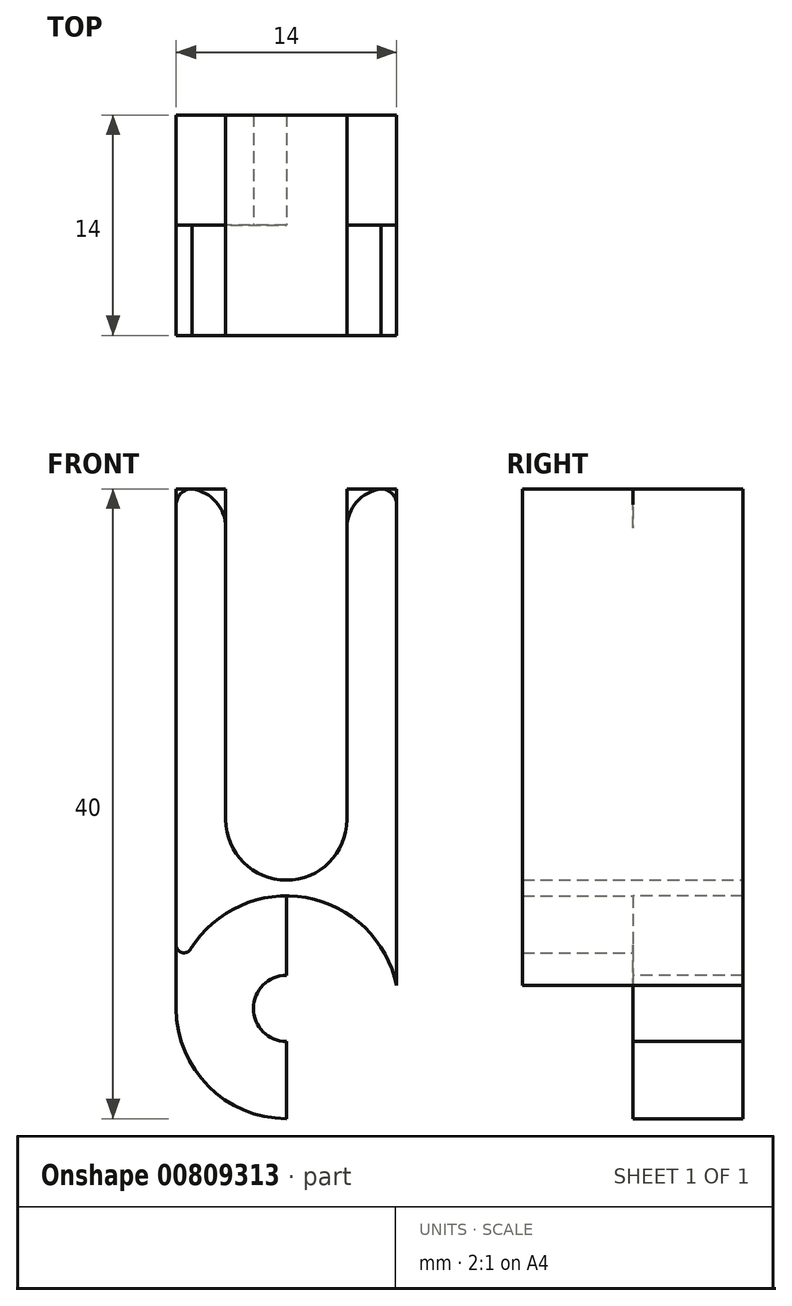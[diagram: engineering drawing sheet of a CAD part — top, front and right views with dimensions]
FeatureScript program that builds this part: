
annotation { "Feature Type Name" : "Feature", "Feature Type Description" : "" }
export const myFeature = defineFeature(function(context is Context, id is Id, definition is map)
    precondition{}
    {
        {
            var Q0;
            Q0=qCreatedBy(makeId("Front.planeOp"),FACE);
            var sketch = newSketch(context, id + "F0", { "sketchPlane" : qUnion([Q0])});
            skArc(sketch, "E0", {"start": v(0, 7) * mm, "mid": v(-7, 0) * mm, "end": v(0, -7) * mm});
            skLineSegment(sketch, "E1", {"start": v(-7, 0) * mm, "end": v(-7, 33) * mm});
            skLineSegment(sketch, "E2", {"start": v(0, 7.15) * mm, "end": v(0, 7) * mm});
            skArc(sketch, "E3", {"start": v(0, 7.15) * mm, "mid": v(-4.51, 5.55) * mm, "end": v(-7, 1.46) * mm});
            skLineSegment(sketch, "E4", {"start": v(0, 7.15) * mm, "end": v(0, -7) * mm});
            skPoint(sketch, "E5.orphan", {"position": v(7, 0) * mm});
            skLineSegment(sketch, "E6", {"start": v(-3.85, 12) * mm, "end": v(-3.85, 33) * mm});
            skArc(sketch, "E7.MirrorCS", {"start": v(0, 7.15) * mm, "mid": v(4.51, 5.55) * mm, "end": v(7, 1.46) * mm});
            skArc(sketch, "E8.MirrorCS", {"start": v(0, 7) * mm, "mid": v(7, 0) * mm, "end": v(0, -7) * mm});
            skArc(sketch, "E9.MirrorCS", {"start": v(3.85, 12) * mm, "mid": v(2.72, 9.28) * mm, "end": v(0, 8.15) * mm});
            skLineSegment(sketch, "E10.MirrorCS", {"start": v(7, 0) * mm, "end": v(7, 33) * mm});
            skLineSegment(sketch, "E11.MirrorCS", {"start": v(3.85, 12) * mm, "end": v(3.85, 33) * mm});
            skArc(sketch, "E12", {"start": v(-3.85, 12) * mm, "mid": v(-2.72, 9.28) * mm, "end": v(0, 8.15) * mm});
            skLineSegment(sketch, "E13", {"start": v(-7, 33) * mm, "end": v(-3.85, 33) * mm});
            skLineSegment(sketch, "E14", {"start": v(3.85, 33) * mm, "end": v(7, 33) * mm});
            skSolve(sketch);
        }
        {
            var Q0;
            {var subQ0=sQuery(id+"F0.wireOp",EDGE,"E3");Q0=makeQuery(id+"F0.imprint","IMPRINT",FACE,{"disambiguationData":[TD([[makeQuery(id+"F0.imprint","IMPRINT",EDGE,{"derivedFrom":subQ0}),-1.0]])]});}
            extrude(context, id + "F1", {"entities" : qUnion([Q0]), "endBound" : BoundingType.SYMMETRIC, "depth" : 14 * mm, "offsetDistance" : 25 * mm});
        }
        {
            var Q0;
            Q0=makeQuery(id+"F1.opExtrude","SWEPT_EDGE",EDGE,{"disambiguationData":[OSD([sQuery(id+"F0.wireOp",EDGE,"E1"),sQuery(id+"F0.wireOp",EDGE,"E13")])]});
            var Q1;
            Q1=makeQuery(id+"F1.opExtrude","SWEPT_EDGE",EDGE,{"disambiguationData":[OSD([sQuery(id+"F0.wireOp",EDGE,"E10.MirrorCS"),sQuery(id+"F0.wireOp",EDGE,"E14")])]});
            fillet(context, id + "F2", {"entities" : qUnion([Q0, Q1]), "radius" : 1 * mm, "tangentPropagation" : true, "allowEdgeOverflow" : false});
        }
        {
            var Q0;
            Q0=makeQuery(id+"F1.opExtrude","SWEPT_EDGE",EDGE,{"disambiguationData":[OSD([sQuery(id+"F0.wireOp",EDGE,"E6"),sQuery(id+"F0.wireOp",EDGE,"E13")])]});
            var Q1;
            Q1=makeQuery(id+"F1.opExtrude","SWEPT_EDGE",EDGE,{"disambiguationData":[OSD([sQuery(id+"F0.wireOp",EDGE,"E11.MirrorCS"),sQuery(id+"F0.wireOp",EDGE,"E14")])]});
            fillet(context, id + "F3", {"entities" : qUnion([Q0, Q1]), "radius" : 2.5 * mm, "tangentPropagation" : true, "allowEdgeOverflow" : false});
        }
        {
            var Q0;
            {var subQ5=sQuery(id+"F0.wireOp",EDGE,"E3");Q0=makeQuery(id+"F0.imprint","IMPRINT",FACE,{"disambiguationData":[TD([[makeQuery(id+"F0.imprint","IMPRINT",EDGE,{"derivedFrom":subQ5}),1.0]])]});}
            var Q1;
            {var subQ3=sQuery(id+"F0.wireOp",EDGE,"E7.MirrorCS");Q1=makeQuery(id+"F0.imprint","IMPRINT",FACE,{"disambiguationData":[TD([[makeQuery(id+"F0.imprint","IMPRINT",EDGE,{"derivedFrom":subQ3}),-1.0]])]});}
            var Q2;
            {var subQ0=sQuery(id+"F0.wireOp",EDGE,"E8.MirrorCS");var subQ5=makeQuery(id+"F0.imprint","INTERSECT",VERTEX,{"derivedFrom":[subQ0,sQuery(id+"F0.wireOp",EDGE,"E10.MirrorCS")]});Q2=makeQuery(id+"F0.imprint","IMPRINT",FACE,{"disambiguationData":[TD([[makeQuery(id+"F0.imprint","IMPRINT",EDGE,{"disambiguationData":[TD([[subQ5,1.0]])],"derivedFrom":subQ0}),-1.0]])]});}
            var Q3;
            {var subQ2=sQuery(id+"F0.wireOp",EDGE,"E0");var subQ4=makeQuery(id+"F0.imprint","INTERSECT",VERTEX,{"derivedFrom":[subQ2,sQuery(id+"F0.wireOp",EDGE,"E1")]});Q3=makeQuery(id+"F0.imprint","IMPRINT",FACE,{"disambiguationData":[TD([[makeQuery(id+"F0.imprint","IMPRINT",EDGE,{"disambiguationData":[TD([[subQ4,1.0]])],"derivedFrom":subQ2}),1.0]])]});}
            extrude(context, id + "F4", {"entities" : qUnion([Q0, Q1, Q2, Q3]), "operationType" : NewBodyOperationType.ADD, "oppositeDirection" : true, "depth" : 7 * mm, "offsetDistance" : 25 * mm});
        }
        {
            var Q0;
            Q0=sQuery(id+"F0.wireOp",VERTEX,"E0.center");
            var Q1;
            Q1=makeQuery(id+"F1.opExtrude","SWEPT_BODY",BODY,{"disambiguationData":[OSD([sQuery(id+"F0.wireOp",EDGE,"E1"),sQuery(id+"F0.wireOp",EDGE,"E3"),sQuery(id+"F0.wireOp",EDGE,"E6"),sQuery(id+"F0.wireOp",EDGE,"E7.MirrorCS"),sQuery(id+"F0.wireOp",EDGE,"E9.MirrorCS"),sQuery(id+"F0.wireOp",EDGE,"E10.MirrorCS"),sQuery(id+"F0.wireOp",EDGE,"E11.MirrorCS"),sQuery(id+"F0.wireOp",EDGE,"E12"),sQuery(id+"F0.wireOp",EDGE,"E13"),sQuery(id+"F0.wireOp",EDGE,"E14")])]});
            hole(context, id + "F5", {"style" : HoleStyle.SIMPLE, "endStyle" : HoleEndStyle.THROUGH, "holeDiameter" : 4.2 * mm, "majorDiameter" : 5 * mm, "isTappedThrough" : true, "tappedDepth" : 12 * mm, "tapClearance" : 3, "locations" : qUnion([Q0]), "scope" : qUnion([Q1])});
        }
        {
            var Q0;
            Q0=makeQuery(id+"F1.opExtrude","SWEPT_EDGE",EDGE,{"disambiguationData":[OSD([sQuery(id+"F0.wireOp",EDGE,"E1"),sQuery(id+"F0.wireOp",EDGE,"E3")])]});
            fillet(context, id + "F6", {"entities" : qUnion([Q0]), "radius" : .5 * mm, "tangentPropagation" : true, "allowEdgeOverflow" : false});
        }
    });
